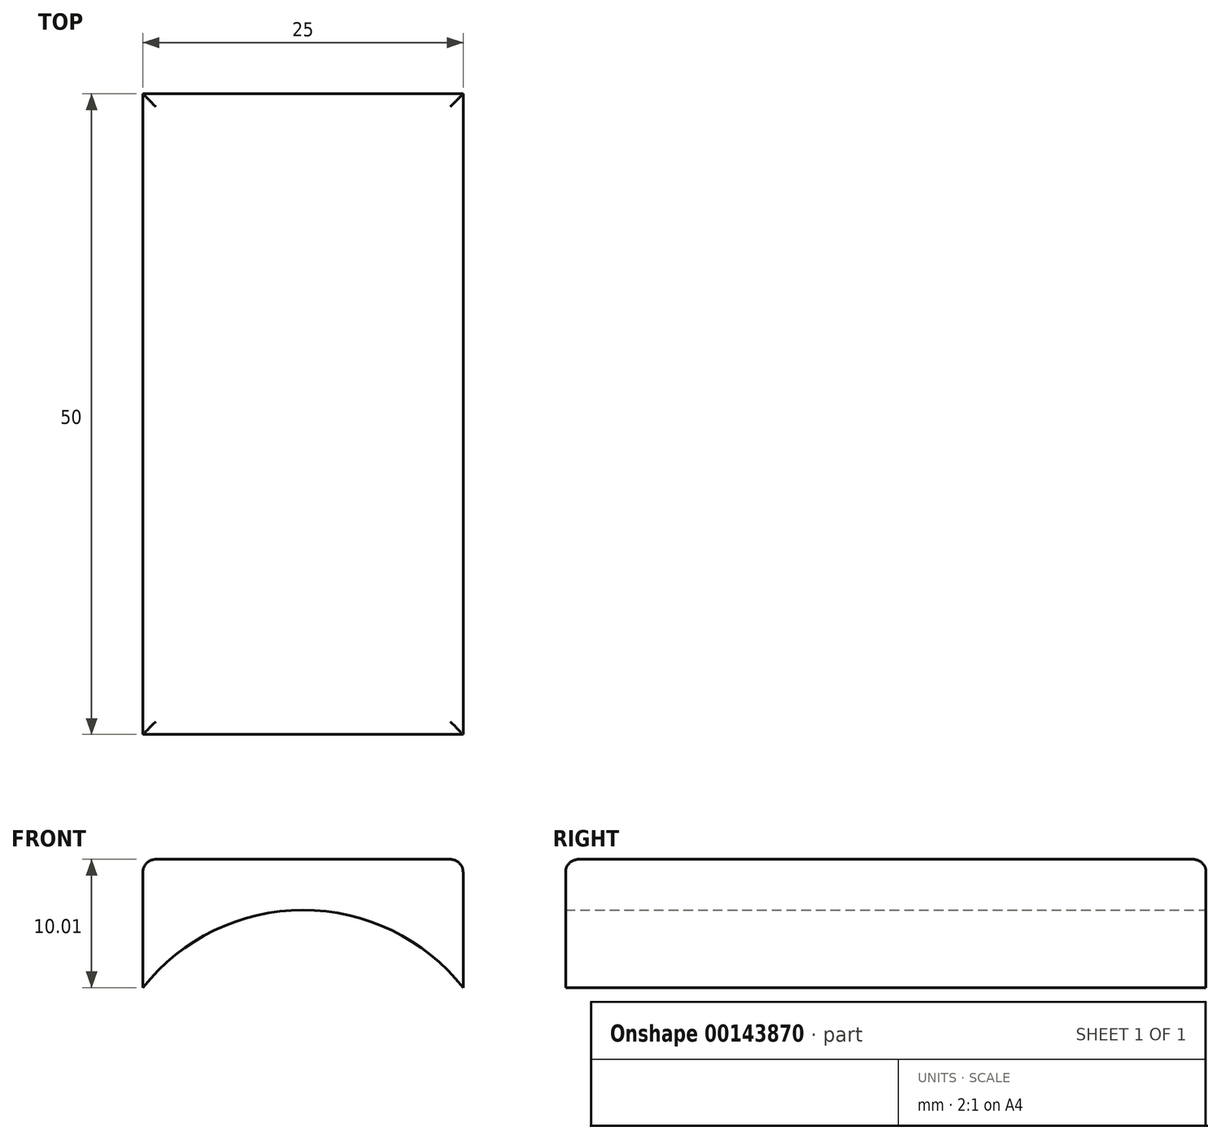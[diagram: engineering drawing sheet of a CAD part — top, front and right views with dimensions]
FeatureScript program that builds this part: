
annotation { "Feature Type Name" : "Feature", "Feature Type Description" : "" }
export const myFeature = defineFeature(function(context is Context, id is Id, definition is map)
    precondition{}
    {
        {
            var Q0;
            Q0=qCreatedBy(makeId("Front.planeOp"),FACE);
            var sketch = newSketch(context, id + "F0", { "sketchPlane" : qUnion([Q0])});
            skLineSegment(sketch, "E0", {"start": v(0, 20) * mm, "end": v(-12.5, 20) * mm});
            skLineSegment(sketch, "E1", {"start": v(-12.5, 20) * mm, "end": v(12.5, 20) * mm});
            skLineSegment(sketch, "E2", {"start": v(-12.5, 20) * mm, "end": v(-12.5, 9.99) * mm});
            skLineSegment(sketch, "E3", {"start": v(12.5, 20) * mm, "end": v(12.5, 9.99) * mm});
            skArc(sketch, "E4", {"start": v(12.5, 9.99) * mm, "mid": v(0, 16.04) * mm, "end": v(-12.5, 9.99) * mm});
            skSolve(sketch);
        }
        {
            var Q0;
            {var subQ0=sQuery(id+"F0.wireOp",EDGE,"E2");Q0=makeQuery(id+"F0.imprint","IMPRINT",FACE,{"disambiguationData":[TD([[makeQuery(id+"F0.imprint","IMPRINT",EDGE,{"derivedFrom":subQ0}),1.0]])]});}
            extrude(context, id + "F1", {"entities" : qUnion([Q0]), "depth" : 50 * mm, "offsetDistance" : 25 * mm});
        }
        {
            var Q0;
            Q0=makeQuery(id+"F1.opExtrude","SWEPT_FACE",FACE,{"disambiguationData":[OSD([sQuery(id+"F0.wireOp",EDGE,"E1")])]});
            fillet(context, id + "F2", {"entities" : qUnion([Q0]), "radius" : 1 * mm, "tangentPropagation" : true, "allowEdgeOverflow" : false});
        }
    });
